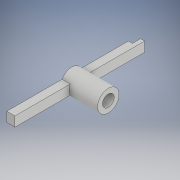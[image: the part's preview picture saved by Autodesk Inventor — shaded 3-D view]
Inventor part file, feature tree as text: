
AUTODESK INVENTOR PART (.ipt)
format: ipt  version: 2019 (Build 230136000, 136)  size: 161,792 bytes
history: native  units: in
note: dims shown in document units (in); Inventor stores cm internally (conversion verified against a paired STEP export)
features: sketch x7, extrude x6, projected_geometry x3
ambient origin geometry x8: Origin, YZ Plane, XZ Plane, XY Plane, X Axis, Y Axis, Z Axis, Center Point
bodies: Solid1 (feature_tree)
feature tree (16):
  extrude  "Extrusion1"  Depth=0.36in
  extrude  "Extrusion2"  Depth=0.1in TaperAngle=0.0deg
  extrude  "Extrusion7"  TaperAngle=0.0deg  [1 undecoded]
  extrude  "Extrusion18"  TaperAngle=0.0deg  [1 undecoded]
  extrude  "Extrusion19"  Depth=4.0in
  extrude  "Extrusion20"  Depth=0.15in
  sketch  "Sketch27"  dims[d94=0.25in d95=0.0in d96=0.25in d97=0.0in d98=0.125in d99=0.25in d100=1.0in d101=0.0in]
  sketch  "Sketch1"  dims[d0=0.36in d1=0.15in]
  sketch  "Sketch2"  dims[d2=0.78in d3=0.0in d4=0.1in d5=0.0in]
  sketch  "Sketch10"  dims[d28=0.875in d29=0.0in d42=0.0in]
  sketch  "Sketch24"  dims[d43=0.0in d44=0.0in]
  projected_geometry  "Projected Loop15"
  sketch  "Sketch25"  dims[d90=4.0in d91=2.0in]
  projected_geometry  "Projected Loop16"
  projected_geometry  "Projected Loop17"
  sketch  "Sketch26"  dims[d92=0.15in d93=0.15in]
note: 2 required parameter values undecoded (feature->parameter linkage not recoverable at this tier; creation-order binding heuristic only, values carry confidence <= 0.55)
